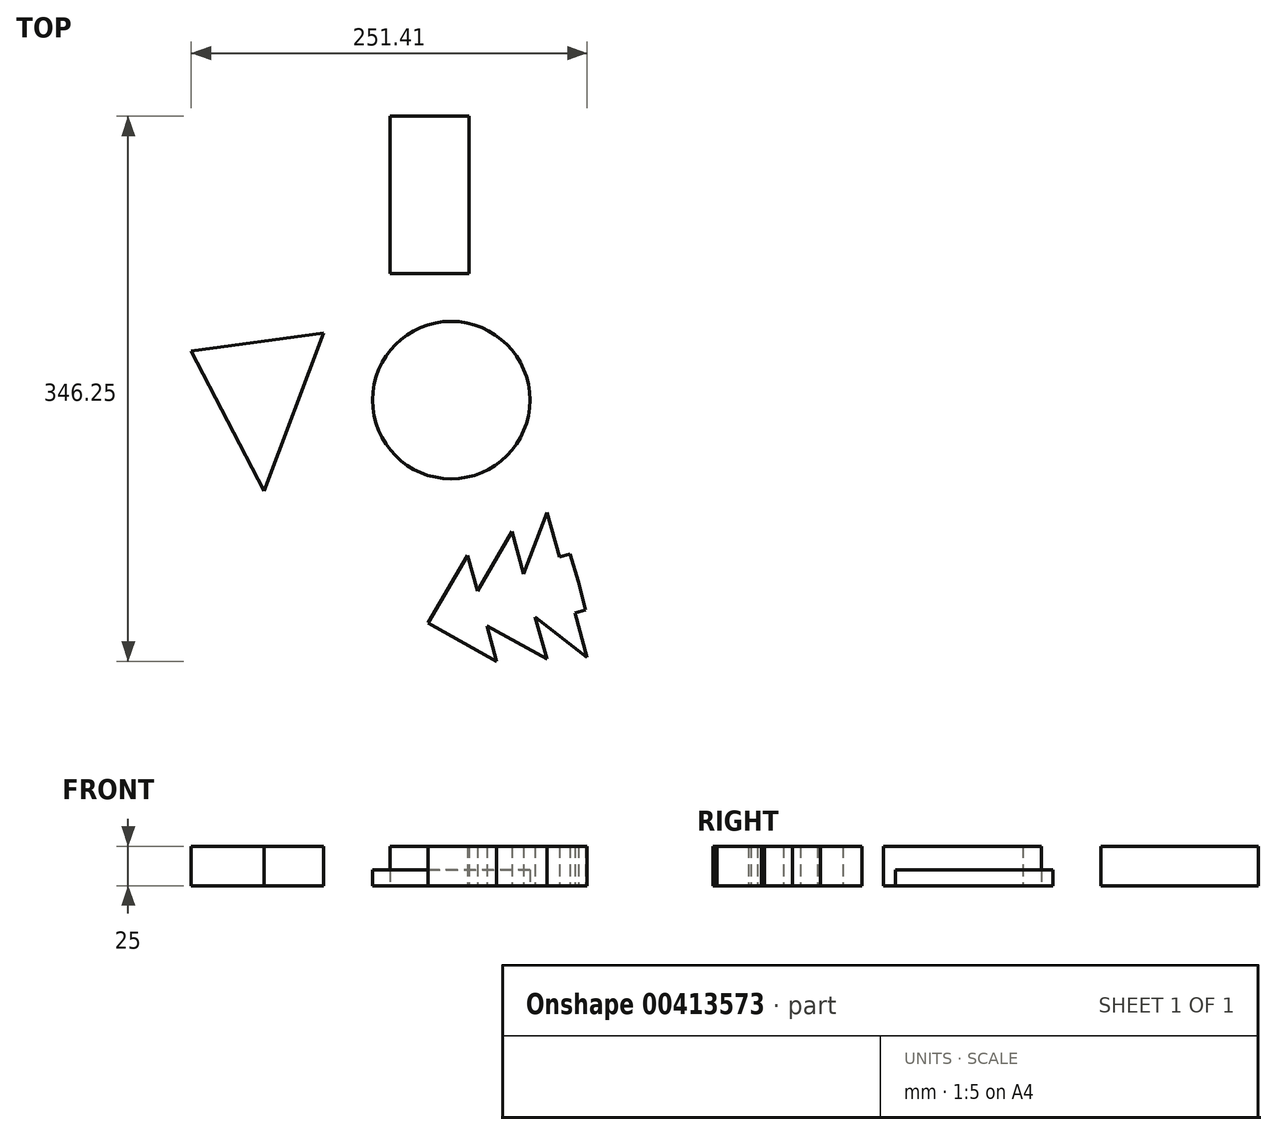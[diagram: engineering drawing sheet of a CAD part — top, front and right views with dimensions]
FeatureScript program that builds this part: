
annotation { "Feature Type Name" : "Feature", "Feature Type Description" : "" }
export const myFeature = defineFeature(function(context is Context, id is Id, definition is map)
    precondition{}
    {
        {
            var Q0;
            Q0=qCreatedBy(makeId("Top.planeOp"),FACE);
            var sketch = newSketch(context, id + "F0", { "sketchPlane" : qUnion([Q0])});
            skCircle(sketch, "E0", {"center": v(0, 0) * mm, "radius": 50 * mm});
            skSolve(sketch);
        }
        {
            var Q0;
            Q0=makeQuery(id+"F0.imprint","IMPRINT",FACE,{"disambiguationData":[TD([[makeQuery(id+"F0.imprint","IMPRINT",EDGE,{"derivedFrom":sQuery(id+"F0.wireOp",EDGE,"E0")}),1.0]])]});
            extrude(context, id + "F1", {"entities" : qUnion([Q0]), "depth" : 10 * mm});
        }
        {
            var Q0;
            Q0=qCreatedBy(makeId("Top.planeOp"),FACE);
            var sketch = newSketch(context, id + "F2", { "sketchPlane" : qUnion([Q0])});
            skLineSegment(sketch, "E1.bottom", {"start": v(11.33, 180.32) * mm, "end": v(-38.67, 180.32) * mm});
            skLineSegment(sketch, "E1.top", {"start": v(11.33, 80.32) * mm, "end": v(-38.67, 80.32) * mm});
            skLineSegment(sketch, "E1.left", {"start": v(11.33, 180.32) * mm, "end": v(11.33, 80.32) * mm});
            skLineSegment(sketch, "E1.right", {"start": v(-38.67, 180.32) * mm, "end": v(-38.67, 80.32) * mm});
            skSolve(sketch);
        }
        {
            var Q0;
            Q0=makeQuery(id+"F2.imprint","IMPRINT",FACE,{"disambiguationData":[TD([[makeQuery(id+"F2.imprint","IMPRINT",EDGE,{"derivedFrom":sQuery(id+"F2.wireOp",EDGE,"E1.bottom")}),1.0]])]});
            extrude(context, id + "F3", {"entities" : qUnion([Q0]), "depth" : 25 * mm});
        }
        {
            var Q0;
            Q0=qCreatedBy(makeId("Top.planeOp"),FACE);
            var sketch = newSketch(context, id + "F4", { "sketchPlane" : qUnion([Q0])});
            skLineSegment(sketch, "E2", {"start": v(-118.76, -57.6) * mm, "end": v(-81.14, 42.56) * mm});
            skLineSegment(sketch, "E3", {"start": v(-81.14, 42.56) * mm, "end": v(-165.1, 31.02) * mm});
            skLineSegment(sketch, "E4", {"start": v(-165.1, 31.02) * mm, "end": v(-118.76, -57.6) * mm});
            skLineSegment(sketch, "E5", {"start": v(-81.14, 42.56) * mm, "end": v(-148.88, 0) * mm, "construction": true});
            skSolve(sketch);
        }
        {
            var Q0;
            Q0=makeQuery(id+"F4.imprint","IMPRINT",FACE,{"disambiguationData":[TD([[makeQuery(id+"F4.imprint","IMPRINT",EDGE,{"derivedFrom":sQuery(id+"F4.wireOp",EDGE,"E2")}),1.0]])]});
            extrude(context, id + "F5", {"entities" : qUnion([Q0]), "depth" : 25 * mm});
        }
        {
            var Q0;
            Q0=qCreatedBy(makeId("Top.planeOp"),FACE);
            var sketch = newSketch(context, id + "F6", { "sketchPlane" : qUnion([Q0])});
            skLineSegment(sketch, "E6", {"start": v(-24.31, -144.35) * mm, "end": v(80.84, -115.48) * mm, "construction": true});
            skLineSegment(sketch, "E7", {"start": v(-14.7, -141.7) * mm, "end": v(28.87, -165.93) * mm});
            skLineSegment(sketch, "E8", {"start": v(28.87, -165.93) * mm, "end": v(22.68, -143.38) * mm});
            skLineSegment(sketch, "E9", {"start": v(22.68, -143.38) * mm, "end": v(60.74, -164.54) * mm});
            skLineSegment(sketch, "E10", {"start": v(60.74, -164.54) * mm, "end": v(53.38, -137.75) * mm});
            skLineSegment(sketch, "E11", {"start": v(53.38, -137.75) * mm, "end": v(86.3, -163.5) * mm});
            skLineSegment(sketch, "E12", {"start": v(86.3, -163.5) * mm, "end": v(78.55, -135.25) * mm});
            skLineSegment(sketch, "E13", {"start": v(78.55, -135.25) * mm, "end": v(85.26, -133.4) * mm});
            skLineSegment(sketch, "E14", {"start": v(85.26, -133.4) * mm, "end": v(80.84, -115.48) * mm});
            skLineSegment(sketch, "E15", {"start": v(-14.7, -141.7) * mm, "end": v(80.84, -115.48) * mm});
            skLineSegment(sketch, "E16.MirrorCS", {"start": v(-14.7, -141.7) * mm, "end": v(10.4, -98.64) * mm});
            skLineSegment(sketch, "E17.MirrorCS", {"start": v(10.4, -98.64) * mm, "end": v(16.58, -121.18) * mm});
            skLineSegment(sketch, "E18.MirrorCS", {"start": v(16.58, -121.18) * mm, "end": v(38.5, -83.56) * mm});
            skLineSegment(sketch, "E19.MirrorCS", {"start": v(38.5, -83.56) * mm, "end": v(45.86, -110.35) * mm});
            skLineSegment(sketch, "E20.MirrorCS", {"start": v(45.86, -110.35) * mm, "end": v(61.02, -71.4) * mm});
            skLineSegment(sketch, "E21.MirrorCS", {"start": v(61.02, -71.4) * mm, "end": v(68.78, -99.65) * mm});
            skLineSegment(sketch, "E22.MirrorCS", {"start": v(68.78, -99.65) * mm, "end": v(75.48, -97.81) * mm});
            skLineSegment(sketch, "E23.MirrorCS", {"start": v(75.48, -97.81) * mm, "end": v(80.84, -115.48) * mm});
            skSolve(sketch);
        }
        {
            var Q0;
            Q0=makeQuery(id+"F6.imprint","IMPRINT",FACE,{"disambiguationData":[TD([[makeQuery(id+"F6.imprint","IMPRINT",EDGE,{"derivedFrom":sQuery(id+"F6.wireOp",EDGE,"E7")}),1.0]])]});
            var Q1;
            Q1=makeQuery(id+"F6.imprint","IMPRINT",FACE,{"disambiguationData":[TD([[makeQuery(id+"F6.imprint","IMPRINT",EDGE,{"derivedFrom":sQuery(id+"F6.wireOp",EDGE,"E15")}),1.0]])]});
            extrude(context, id + "F7", {"entities" : qUnion([Q0, Q1]), "depth" : 25 * mm});
        }
    });
